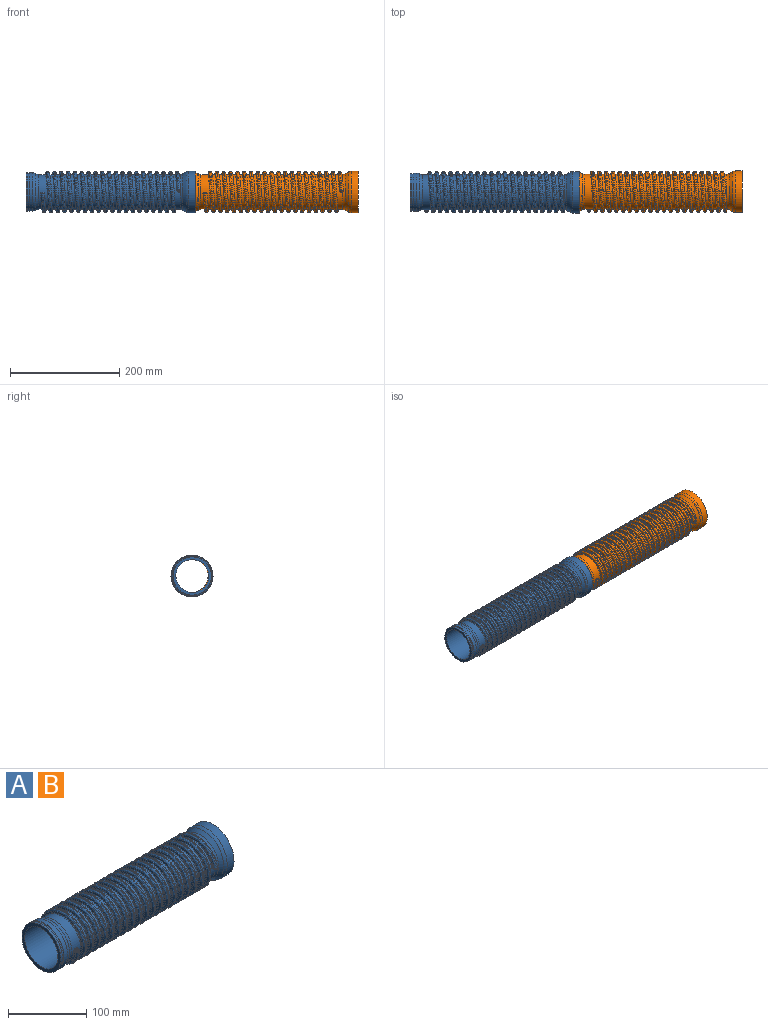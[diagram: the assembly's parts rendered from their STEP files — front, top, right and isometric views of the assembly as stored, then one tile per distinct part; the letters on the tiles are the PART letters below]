
ASSEMBLY  parts=2 mates=1
PART A: 61 faces, bbox 310.6x112.6x112.6 mm
  f0: cylinder r=35mm len=70mm, axis (-1,0,0), area 1390mm2, adj f1,f60
  f1: torus R=25mm, axis (-1,0,0), area 1136.6mm2, adj f0,f2
  f2: cone r=33.34mm half-angle=30deg, axis (-1,0,0), area 134.9mm2, adj f1,f3
  f3: torus R=42mm, axis (-1,0,0), area 1067.6mm2, adj f2,f4
  f4: cylinder r=32mm len=64mm, axis (-1,0,0), area 2608.2mm2, adj f3,f5,f55,f56,f57,f58,f59
  f5: cylinder r=32mm len=64mm, axis (-1,0,0), area 905.1mm2, adj f4,f6,f55,f59
  f6: cylinder r=32mm len=64mm, axis (-1,0,0), area 904.8mm2, adj f5,f7,f55,f59
  f7: cylinder r=32mm len=64mm, axis (-1,0,0), area 905mm2, adj f6,f8,f55,f59
  f8: cylinder r=32mm len=64mm, axis (-1,0,0), area 904.2mm2, adj f7,f9,f55,f59
  f9: cylinder r=32mm len=64mm, axis (-1,0,0), area 904.8mm2, adj f8,f10,f55,f59
  f10: cylinder r=32mm len=64mm, axis (-1,0,0), area 905.4mm2, adj f9,f11,f55,f59
  f11: cylinder r=32mm len=64mm, axis (-1,0,0), area 904.5mm2, adj f10,f12,f55,f59
  f12: cylinder r=32mm len=64mm, axis (-1,0,0), area 904.7mm2, adj f11,f13,f55,f59
  f13: cylinder r=32mm len=64mm, axis (-1,0,0), area 904.6mm2, adj f12,f14,f55,f59
  f14: cylinder r=32mm len=64mm, axis (-1,0,0), area 904.9mm2, adj f13,f15,f55,f59
  f15: cylinder r=32mm len=64mm, axis (-1,0,0), area 905.3mm2, adj f14,f16,f55,f59
  f16: cylinder r=32mm len=64mm, axis (-1,0,0), area 904.3mm2, adj f15,f17,f55,f59
  f17: cylinder r=32mm len=64mm, axis (-1,0,0), area 904.5mm2, adj f16,f18,f55,f59
  f18: cylinder r=32mm len=64mm, axis (-1,0,0), area 905.3mm2, adj f17,f19,f55,f59
  f19: cylinder r=32mm len=64mm, axis (-1,0,0), area 904.7mm2, adj f18,f20,f55,f59
  f20: cylinder r=32mm len=64mm, axis (-1,0,0), area 904.9mm2, adj f19,f21,f55,f59
  f21: cylinder r=32mm len=64mm, axis (-1,0,0), area 904.3mm2, adj f20,f22,f55,f59
  f22: cylinder r=32mm len=64mm, axis (-1,0,0), area 904.8mm2, adj f21,f23,f55,f59
  f23: cylinder r=32mm len=64mm, axis (-1,0,0), area 1155.1mm2, adj f22,f24,f40,f41,f53,f54,f55,f59
  f24: plane 2.91x1.23mm, normal (0,0,-1), area 3mm2, adj f23,f25,f38,f39,f40,f54
  f25: bspline ~2.66x2.51mm, area 7.6mm2, adj f24,f26,f37,f54
  f26: bspline ~250x70mm, area 8518.6mm2, adj f25,f27,f36,f59
  f27: bspline ~3x2.65mm, area 8.2mm2, adj f26,f28,f57,f58
  f28: sphere r=2.5mm, area 10.5mm2, adj f27,f29,f36
  f29: cylinder r=2.5mm len=2.68mm, axis (1,0,0), area 4.1mm2, adj f28,f30,f35,f57
  f30: sphere r=2.5mm, area 6.5mm2, adj f29,f31,f33
  f31: bspline ~3x2.51mm, area 7.6mm2, adj f30,f32,f56,f57
  f32: bspline ~250x70mm, area 8518.9mm2, adj f31,f33,f39,f55
  f33: bspline ~252.5x75mm, area 17985.1mm2, adj f30,f32,f34,f35
  f34: sphere r=2.5mm, area 10.6mm2, adj f33,f38,f39
  f35: cylinder r=37.5mm len=250.73mm, axis (1,0,0), area 4707.3mm2, adj f29,f33,f36,f38
  f36: bspline ~252.5x75mm, area 17985.4mm2, adj f26,f28,f35,f37
  f37: sphere r=2.5mm, area 9.9mm2, adj f25,f36,f38
  f38: cylinder r=2.5mm len=2.68mm, axis (1,0,0), area 4.1mm2, adj f24,f34,f35,f37
  f39: bspline ~3.01x2.65mm, area 8.2mm2, adj f24,f32,f34,f40
  f40: bspline ~3.62x3.34mm, area 4.1mm2, adj f23,f24,f39,f41,f55
  f41: torus R=42mm, axis (-1,0,0), area 1472mm2, adj f23,f40,f42,f53,f55
  f42: cone r=33.34mm half-angle=30deg, axis (1,0,0), area 1460.4mm2, adj f41,f43
  f43: torus R=28mm, axis (-1,0,0), area 1235.3mm2, adj f42,f44
  f44: cylinder r=38mm len=76mm, axis (-1,0,0), area 2941.7mm2, adj f43,f45
  f45: torus R=38mm, axis (-1,0,0), area 725mm2, adj f44,f46
  f46: cylinder r=36mm len=72mm, axis (-1,0,0), area 2940.5mm2, adj f45,f47
  f47: plane 72x72mm, normal (1,0,0), area 1244.1mm2, adj f46,f48
  f48: cylinder r=30mm len=295.59mm, axis (-1,0,0), area 55717.1mm2, adj f47,f49
  f49: plane 70x70mm, normal (-1,0,0), area 1021mm2, adj f48,f50
  f50: cylinder r=35mm len=70mm, axis (-1,0,0), area 659.7mm2, adj f49,f51
  f51: plane 70x70mm, normal (1,0,0), area 216.8mm2, adj f50,f52
  f52: cylinder r=34mm len=68mm, axis (-1,0,0), area 640.9mm2, adj f51,f60
  f53: cylinder r=32mm len=21.2mm, axis (-1,0,0), area 16.7mm2, adj f23,f41,f55
  f54: bspline ~4.27x3.71mm, area 4.1mm2, adj f23,f24,f25,f59
  f55: bspline ~251x66mm, area 6358.4mm2, adj f4,f5,f6,f7,f8,f9,f10,f11
  f56: bspline ~3.61x3.58mm, area 4.1mm2, adj f4,f31,f55,f57
  f57: plane 2.91x1.23mm, normal (0,0,1), area 3mm2, adj f4,f27,f29,f31,f56,f58
  f58: bspline ~3.6x3.54mm, area 4.3mm2, adj f4,f27,f57,f59
  f59: bspline ~251x66mm, area 6384.7mm2, adj f4,f5,f6,f7,f8,f9,f10,f11
  f60: plane 70x70mm, normal (-1,0,0), area 216.8mm2, adj f0,f52
PART B: same geometry as A
PLACE A t=(-252.84,-9.22,139.22)mm
PLACE B t=(44.97,-8.21,139.22)mm
MATE parallel A.f0 <-> B.f0  axis (1,0,0) through (-112.45,-9.22,139.22)mm
